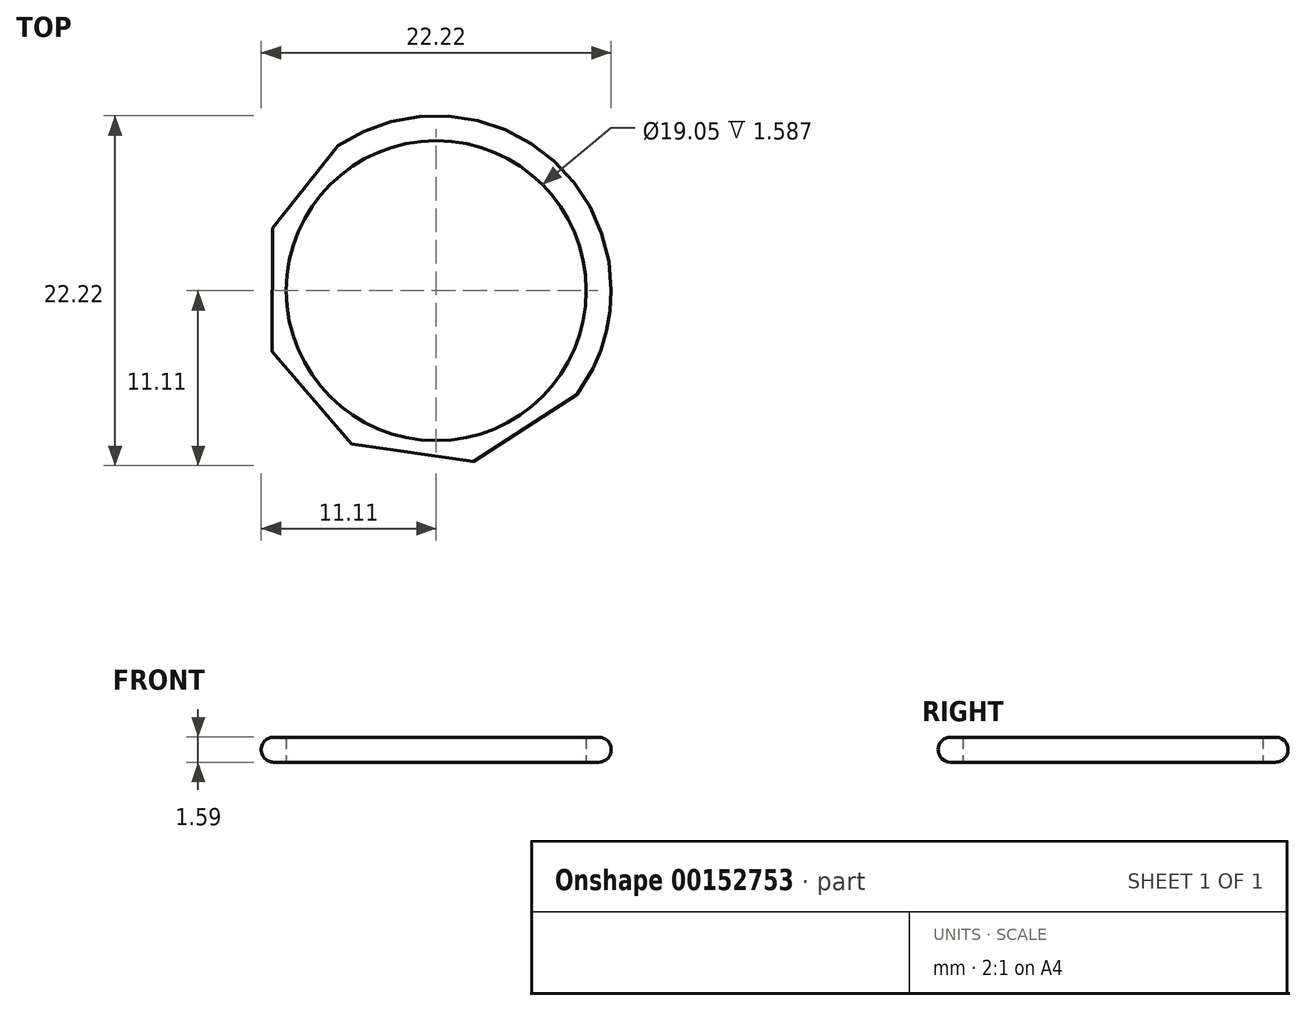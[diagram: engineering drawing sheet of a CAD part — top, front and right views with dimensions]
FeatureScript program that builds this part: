
annotation { "Feature Type Name" : "Feature", "Feature Type Description" : "" }
export const myFeature = defineFeature(function(context is Context, id is Id, definition is map)
    precondition{}
    {
        {
            var Q0;
            Q0=qCreatedBy(makeId("Top.planeOp"),FACE);
            var sketch = newSketch(context, id + "F0", { "sketchPlane" : qUnion([Q0])});
            skCircle(sketch, "E0", {"center": v(0, 0) * mm, "radius": 9.53 * mm});
            skCircle(sketch, "E1", {"center": v(0, 0) * mm, "radius": 11.11 * mm});
            skSolve(sketch);
        }
        {
            var Q0;
            Q0 = qSketchRegion(id + "F0", true);
            extrude(context, id + "F1", {"entities" : qUnion([Q0]), "depth" : 1.59 * mm});
        }
        {
            var Q0;
            Q0=makeQuery(id+"F1.opExtrude","CAP_EDGE",EDGE,{"disambiguationData":[OSD([sQuery(id+"F0.wireOp",EDGE,"E1")])],"isStart":true});
            var Q1;
            Q1=makeQuery(id+"F1.opExtrude","CAP_EDGE",EDGE,{"disambiguationData":[OSD([sQuery(id+"F0.wireOp",EDGE,"E1")])],"isStart":false});
            fillet(context, id + "F2", {"entities" : qUnion([Q0, Q1]), "radius" : 0.8 * mm, "tangentPropagation" : true, "allowEdgeOverflow" : false});
        }
    });
